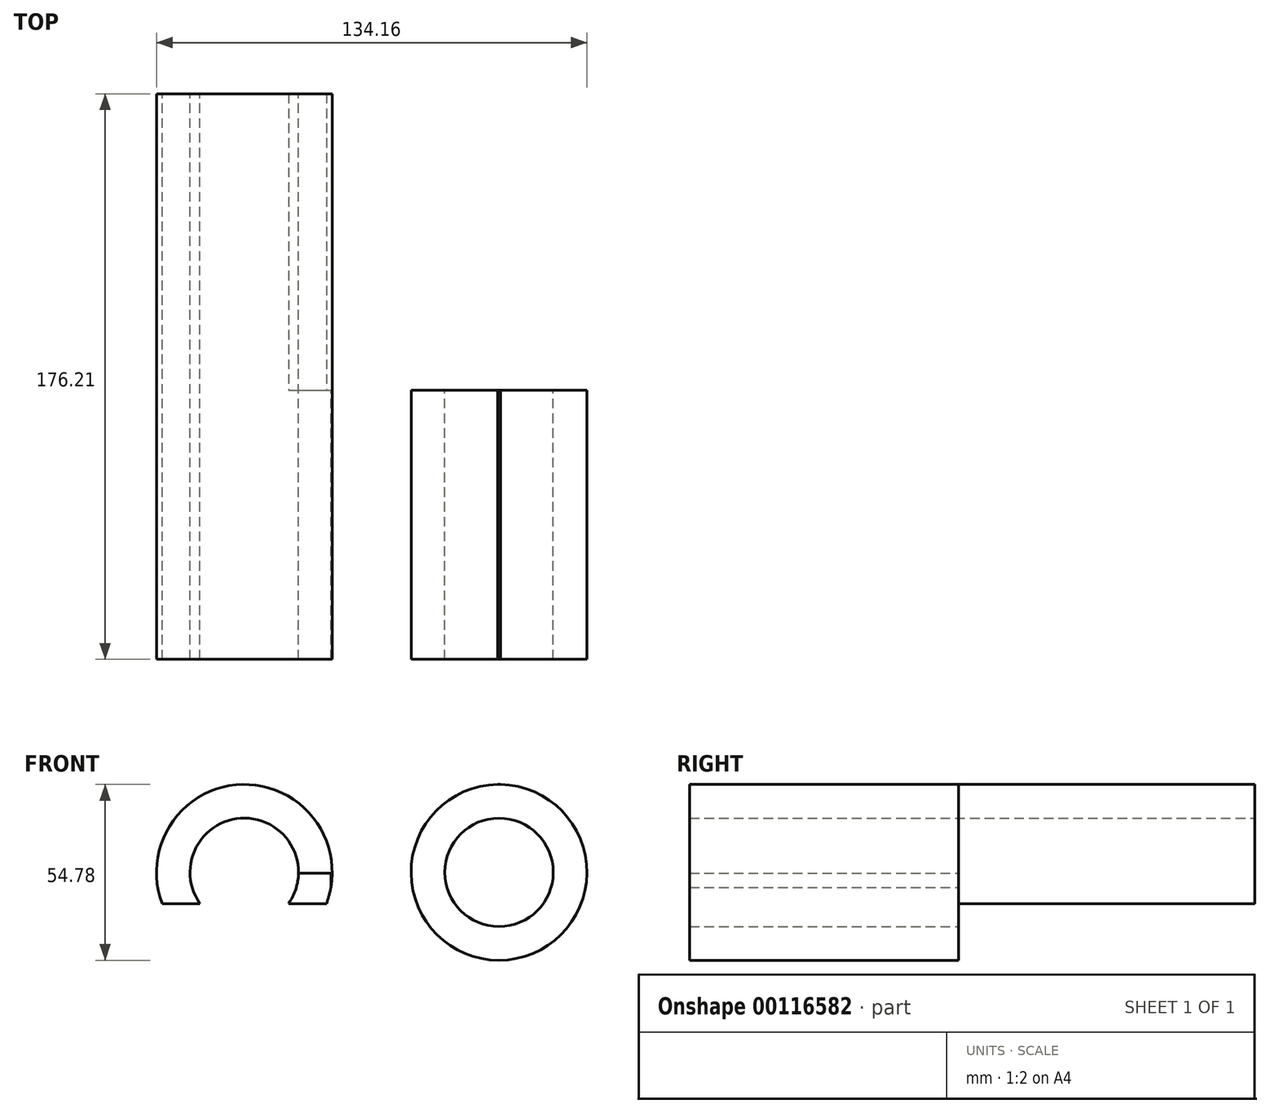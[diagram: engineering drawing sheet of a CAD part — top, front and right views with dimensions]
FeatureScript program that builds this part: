
annotation { "Feature Type Name" : "Feature", "Feature Type Description" : "" }
export const myFeature = defineFeature(function(context is Context, id is Id, definition is map)
    precondition{}
    {
        {
            var Q0;
            Q0=qCreatedBy(makeId("Front.planeOp"),FACE);
            var sketch = newSketch(context, id + "F0", { "sketchPlane" : qUnion([Q0])});
            skCircle(sketch, "E0", {"center": v(0, 0) * mm, "radius": 27.39 * mm});
            skCircle(sketch, "E1", {"center": v(79.38, 0) * mm, "radius": 27.4 * mm});
            skLineSegment(sketch, "E2", {"start": v(0, 27.39) * mm, "end": v(79.83, 27.39) * mm});
            skLineSegment(sketch, "E3", {"start": v(0, -27.39) * mm, "end": v(77.38, -27.32) * mm});
            skCircle(sketch, "E4", {"center": v(0, 0) * mm, "radius": 16.9 * mm});
            skCircle(sketch, "E5", {"center": v(79.38, 0) * mm, "radius": 16.9 * mm});
            skLineSegment(sketch, "E6.bottom", {"start": v(-26.99, -9.74) * mm, "end": v(26.99, -9.74) * mm});
            skLineSegment(sketch, "E6.top", {"start": v(-26.99, -0.21) * mm, "end": v(26.99, -0.21) * mm});
            skLineSegment(sketch, "E6.left", {"start": v(-26.99, -9.74) * mm, "end": v(-26.99, -0.21) * mm});
            skLineSegment(sketch, "E6.right", {"start": v(26.99, -9.74) * mm, "end": v(26.99, -0.21) * mm});
            skPoint(sketch, "E6.middle", {"position": v(0, -4.97) * mm});
            skSolve(sketch);
        }
        {
            var Q0;
            {var subQ4=sQuery(id+"F0.wireOp",EDGE,"E3");var subQ5=sQuery(id+"F0.wireOp",EDGE,"E0");var subQ6=makeQuery(id+"F0.imprint","INTERSECT",VERTEX,{"disambiguationData":[OD(0.0)],"derivedFrom":[subQ5,subQ4]});Q0=makeQuery(id+"F0.imprint","IMPRINT",FACE,{"disambiguationData":[TD([[makeQuery(id+"F0.imprint","IMPRINT",EDGE,{"disambiguationData":[TD([[subQ6,1.0]])],"derivedFrom":subQ5}),1.0]])]});}
            var Q1;
            {var subQ5=sQuery(id+"F0.wireOp",EDGE,"E0");var subQ6=makeQuery(id+"F0.imprint","INTERSECT",VERTEX,{"derivedFrom":[subQ5,sQuery(id+"F0.wireOp",EDGE,"E2")]});Q1=makeQuery(id+"F0.imprint","IMPRINT",FACE,{"disambiguationData":[TD([[makeQuery(id+"F0.imprint","IMPRINT",EDGE,{"disambiguationData":[TD([[subQ6,-1.0]])],"derivedFrom":subQ5}),1.0]])]});}
            var Q2;
            Q2=makeQuery(id+"F0.imprint","IMPRINT",FACE,{"disambiguationData":[TD([[makeQuery(id+"F0.imprint","IMPRINT",EDGE,{"derivedFrom":sQuery(id+"F0.wireOp",EDGE,"E5")}),-1.0]])]});
            var Q3;
            {var subQ1=sQuery(id+"F0.wireOp",EDGE,"E0");var subQ5=sQuery(id+"F0.wireOp",EDGE,"E3");var subQ9=makeQuery(id+"F0.imprint","INTERSECT",VERTEX,{"disambiguationData":[OD(1.0)],"derivedFrom":[subQ1,subQ5]});Q3=makeQuery(id+"F0.imprint","IMPRINT",FACE,{"disambiguationData":[TD([[makeQuery(id+"F0.imprint","IMPRINT",EDGE,{"disambiguationData":[TD([[subQ9,-1.0]])],"derivedFrom":subQ1}),-1.0]])]});}
            var Q4;
            {var subQ0=sQuery(id+"F0.wireOp",EDGE,"E6.left");var subQ6=sQuery(id+"F0.wireOp",EDGE,"E0");var subQ9=makeQuery(id+"F0.imprint","INTERSECT",VERTEX,{"derivedFrom":[subQ6,subQ0]});Q4=makeQuery(id+"F0.imprint","IMPRINT",FACE,{"disambiguationData":[TD([[makeQuery(id+"F0.imprint","IMPRINT",EDGE,{"disambiguationData":[TD([[subQ9,-1.0]])],"derivedFrom":subQ6}),1.0]])]});}
            extrude(context, id + "F1", {"entities" : qUnion([Q0, Q1, Q2, Q3, Q4]), "depth" : 83.8 * mm});
        }
        {
            var Q0;
            {var subQ4=sQuery(id+"F0.wireOp",EDGE,"E3");var subQ5=sQuery(id+"F0.wireOp",EDGE,"E0");var subQ6=makeQuery(id+"F0.imprint","INTERSECT",VERTEX,{"disambiguationData":[OD(0.0)],"derivedFrom":[subQ5,subQ4]});Q0=makeQuery(id+"F0.imprint","IMPRINT",FACE,{"disambiguationData":[TD([[makeQuery(id+"F0.imprint","IMPRINT",EDGE,{"disambiguationData":[TD([[subQ6,1.0]])],"derivedFrom":subQ5}),1.0]])]});}
            var Q1;
            {var subQ5=sQuery(id+"F0.wireOp",EDGE,"E0");var subQ6=makeQuery(id+"F0.imprint","INTERSECT",VERTEX,{"derivedFrom":[subQ5,sQuery(id+"F0.wireOp",EDGE,"E2")]});Q1=makeQuery(id+"F0.imprint","IMPRINT",FACE,{"disambiguationData":[TD([[makeQuery(id+"F0.imprint","IMPRINT",EDGE,{"disambiguationData":[TD([[subQ6,-1.0]])],"derivedFrom":subQ5}),1.0]])]});}
            var Q2;
            {var subQ0=sQuery(id+"F0.wireOp",EDGE,"E6.left");var subQ6=sQuery(id+"F0.wireOp",EDGE,"E0");var subQ9=makeQuery(id+"F0.imprint","INTERSECT",VERTEX,{"derivedFrom":[subQ6,subQ0]});Q2=makeQuery(id+"F0.imprint","IMPRINT",FACE,{"disambiguationData":[TD([[makeQuery(id+"F0.imprint","IMPRINT",EDGE,{"disambiguationData":[TD([[subQ9,-1.0]])],"derivedFrom":subQ6}),1.0]])]});}
            var Q3;
            {var subQ5=sQuery(id+"F0.wireOp",EDGE,"E6.bottom");var subQ7=sQuery(id+"F0.wireOp",EDGE,"E0");var subQ8=makeQuery(id+"F0.imprint","INTERSECT",VERTEX,{"disambiguationData":[OD(1.0)],"derivedFrom":[subQ7,subQ5]});Q3=makeQuery(id+"F0.imprint","IMPRINT",FACE,{"disambiguationData":[TD([[makeQuery(id+"F0.imprint","IMPRINT",EDGE,{"disambiguationData":[TD([[subQ8,-1.0]])],"derivedFrom":subQ7}),1.0]])]});}
            extrude(context, id + "F2", {"entities" : qUnion([Q0, Q1, Q2, Q3]), "operationType" : NewBodyOperationType.ADD, "oppositeDirection" : true, "depth" : 92.4 * mm});
        }
    });
